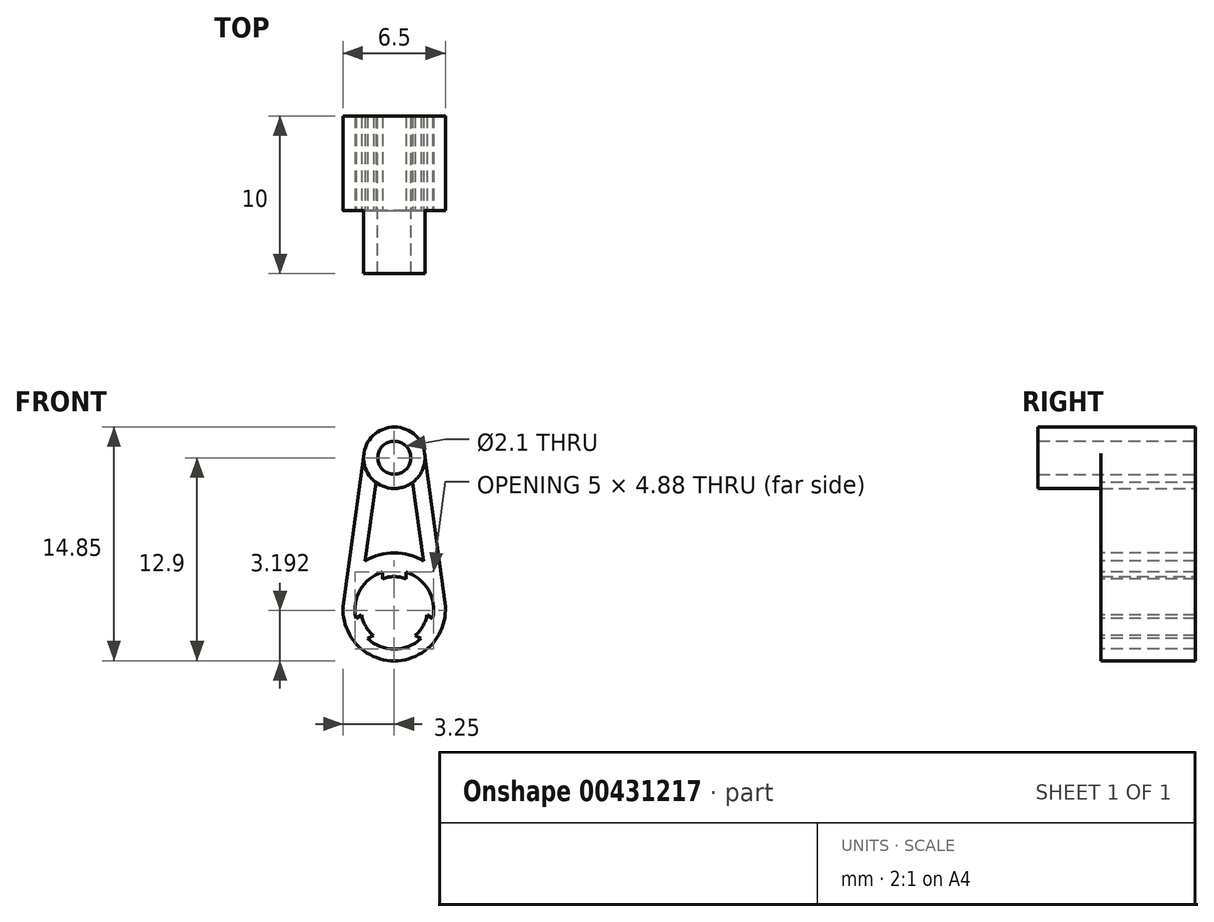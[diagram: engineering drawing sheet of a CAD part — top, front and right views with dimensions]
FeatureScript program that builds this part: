
annotation { "Feature Type Name" : "Feature", "Feature Type Description" : "" }
export const myFeature = defineFeature(function(context is Context, id is Id, definition is map)
    precondition{}
    {
        {
            var Q0;
            Q0=qCreatedBy(makeId("Front.planeOp"),FACE);
            var sketch = newSketch(context, id + "F0", { "sketchPlane" : qUnion([Q0])});
            skArc(sketch, "E0", {"start": v(-3.22, 0.44) * mm, "mid": v(0, -3.25) * mm, "end": v(3.22, 0.44) * mm});
            skArc(sketch, "E1", {"start": v(1.93, 9.91) * mm, "mid": v(0, 11.6) * mm, "end": v(-1.93, 9.91) * mm});
            skLineSegment(sketch, "E2", {"start": v(-1.93, 9.91) * mm, "end": v(-3.22, 0.44) * mm});
            skLineSegment(sketch, "E3", {"start": v(3.22, 0.44) * mm, "end": v(1.93, 9.91) * mm});
            skCircle(sketch, "E4", {"center": v(0, 9.65) * mm, "radius": 1.05 * mm});
            skCircle(sketch, "E5", {"center": v(0, 0) * mm, "radius": 2.1 * mm});
            skSolve(sketch);
        }
        {
            var Q0;
            Q0 = qSketchRegion(id + "F0", true);
            extrude(context, id + "F1", {"entities" : qUnion([Q0]), "depth" : 6 * mm});
        }
        {
            var Q0;
            Q0=makeQuery(id+"F1.opExtrude","CAP_FACE",FACE,{"disambiguationData":[OSD([sQuery(id+"F0.wireOp",EDGE,"E0"),sQuery(id+"F0.wireOp",EDGE,"E1"),sQuery(id+"F0.wireOp",EDGE,"E2"),sQuery(id+"F0.wireOp",EDGE,"E3"),sQuery(id+"F0.wireOp",EDGE,"E4"),sQuery(id+"F0.wireOp",EDGE,"E5")])],"isStart":false});
            var sketch = newSketch(context, id + "F2", { "sketchPlane" : qUnion([Q0])});
            skLineSegment(sketch, "E6.0", {"start": v(-1.17, 8.1) * mm, "end": v(-1.85, 3.09) * mm});
            skLineSegment(sketch, "E7.0", {"start": v(1.85, 3.09) * mm, "end": v(1.17, 8.1) * mm});
            skArc(sketch, "E8.0", {"start": v(-1.17, 8.1) * mm, "mid": v(0, 7.7) * mm, "end": v(1.17, 8.1) * mm});
            skArc(sketch, "E9.0", {"start": v(1.85, 3.09) * mm, "mid": v(0, 3.6) * mm, "end": v(-1.85, 3.09) * mm});
            skSolve(sketch);
        }
        {
            var Q0;
            Q0 = qSketchRegion(id + "F2", true);
            extrude(context, id + "F3", {"entities" : qUnion([Q0]), "operationType" : NewBodyOperationType.REMOVE, "oppositeDirection" : true, "depth" : 25 * mm});
        }
        {
            var Q0;
            Q0=makeQuery(id+"F1.opExtrude","CAP_FACE",FACE,{"disambiguationData":[OSD([sQuery(id+"F0.wireOp",EDGE,"E0"),sQuery(id+"F0.wireOp",EDGE,"E1"),sQuery(id+"F0.wireOp",EDGE,"E2"),sQuery(id+"F0.wireOp",EDGE,"E3"),sQuery(id+"F0.wireOp",EDGE,"E4"),sQuery(id+"F0.wireOp",EDGE,"E5")])],"isStart":false});
            var sketch = newSketch(context, id + "F4", { "sketchPlane" : qUnion([Q0])});
            skArc(sketch, "E10", {"start": v(-0.75, 2.38) * mm, "mid": v(-2.17, 1.25) * mm, "end": v(-2.44, -0.54) * mm});
            skLineSegment(sketch, "E11", {"start": v(-0.75, 2.38) * mm, "end": v(-0.75, 1.96) * mm});
            skLineSegment(sketch, "E12", {"start": v(-2.07, -0.33) * mm, "end": v(-2.44, -0.54) * mm});
            skLineSegment(sketch, "E13", {"start": v(0, 0) * mm, "end": v(-5.4, -3.12) * mm, "construction": true});
            skLineSegment(sketch, "E14", {"start": v(0, 0) * mm, "end": v(0, 5.65) * mm, "construction": true});
            skArc(sketch, "E15", {"start": v(-0.75, 1.96) * mm, "mid": v(-1.82, 1.05) * mm, "end": v(-2.07, -0.33) * mm});
            skArc(sketch, "E16.1.0", {"start": v(-1.32, -1.63) * mm, "mid": v(0, -2.1) * mm, "end": v(1.32, -1.63) * mm});
            skArc(sketch, "E16.1.1", {"start": v(-1.7, -1.84) * mm, "mid": v(0, -2.5) * mm, "end": v(1.7, -1.84) * mm});
            skLineSegment(sketch, "E16.1.2", {"start": v(-1.7, -1.84) * mm, "end": v(-1.32, -1.63) * mm});
            skLineSegment(sketch, "E16.1.3", {"start": v(1.32, -1.63) * mm, "end": v(1.7, -1.84) * mm});
            skArc(sketch, "E16.2.0", {"start": v(2.07, -0.33) * mm, "mid": v(1.82, 1.05) * mm, "end": v(0.75, 1.96) * mm});
            skArc(sketch, "E16.2.1", {"start": v(2.44, -0.54) * mm, "mid": v(2.17, 1.25) * mm, "end": v(0.75, 2.38) * mm});
            skLineSegment(sketch, "E16.2.2", {"start": v(2.44, -0.54) * mm, "end": v(2.07, -0.33) * mm});
            skLineSegment(sketch, "E16.2.3", {"start": v(0.75, 1.96) * mm, "end": v(0.75, 2.38) * mm});
            skPoint(sketch, "E17.orphan", {"position": v(-1.39, 0.06) * mm});
            skPoint(sketch, "E18.orphan", {"position": v(0.75, 1.17) * mm});
            skPoint(sketch, "E19.orphan", {"position": v(0.64, -1.23) * mm});
            skSolve(sketch);
        }
        {
            var Q0;
            Q0 = qSketchRegion(id + "F4", true);
            extrude(context, id + "F5", {"entities" : qUnion([Q0]), "operationType" : NewBodyOperationType.REMOVE, "oppositeDirection" : true, "depth" : 25 * mm});
        }
        {
            var Q0;
            Q0=makeQuery(id+"F1.opExtrude","CAP_FACE",FACE,{"disambiguationData":[OSD([sQuery(id+"F0.wireOp",EDGE,"E0"),sQuery(id+"F0.wireOp",EDGE,"E1"),sQuery(id+"F0.wireOp",EDGE,"E2"),sQuery(id+"F0.wireOp",EDGE,"E3"),sQuery(id+"F0.wireOp",EDGE,"E4"),sQuery(id+"F0.wireOp",EDGE,"E5")])],"isStart":false});
            var sketch = newSketch(context, id + "F6", { "sketchPlane" : qUnion([Q0])});
            skCircle(sketch, "E20", {"center": v(0, 9.65) * mm, "radius": 1.05 * mm});
            skCircle(sketch, "E21", {"center": v(0, 9.65) * mm, "radius": 1.95 * mm});
            skSolve(sketch);
        }
        {
            var Q0;
            Q0 = qSketchRegion(id + "F6", true);
            extrude(context, id + "F7", {"entities" : qUnion([Q0]), "operationType" : NewBodyOperationType.ADD, "depth" : 4 * mm});
        }
    });
